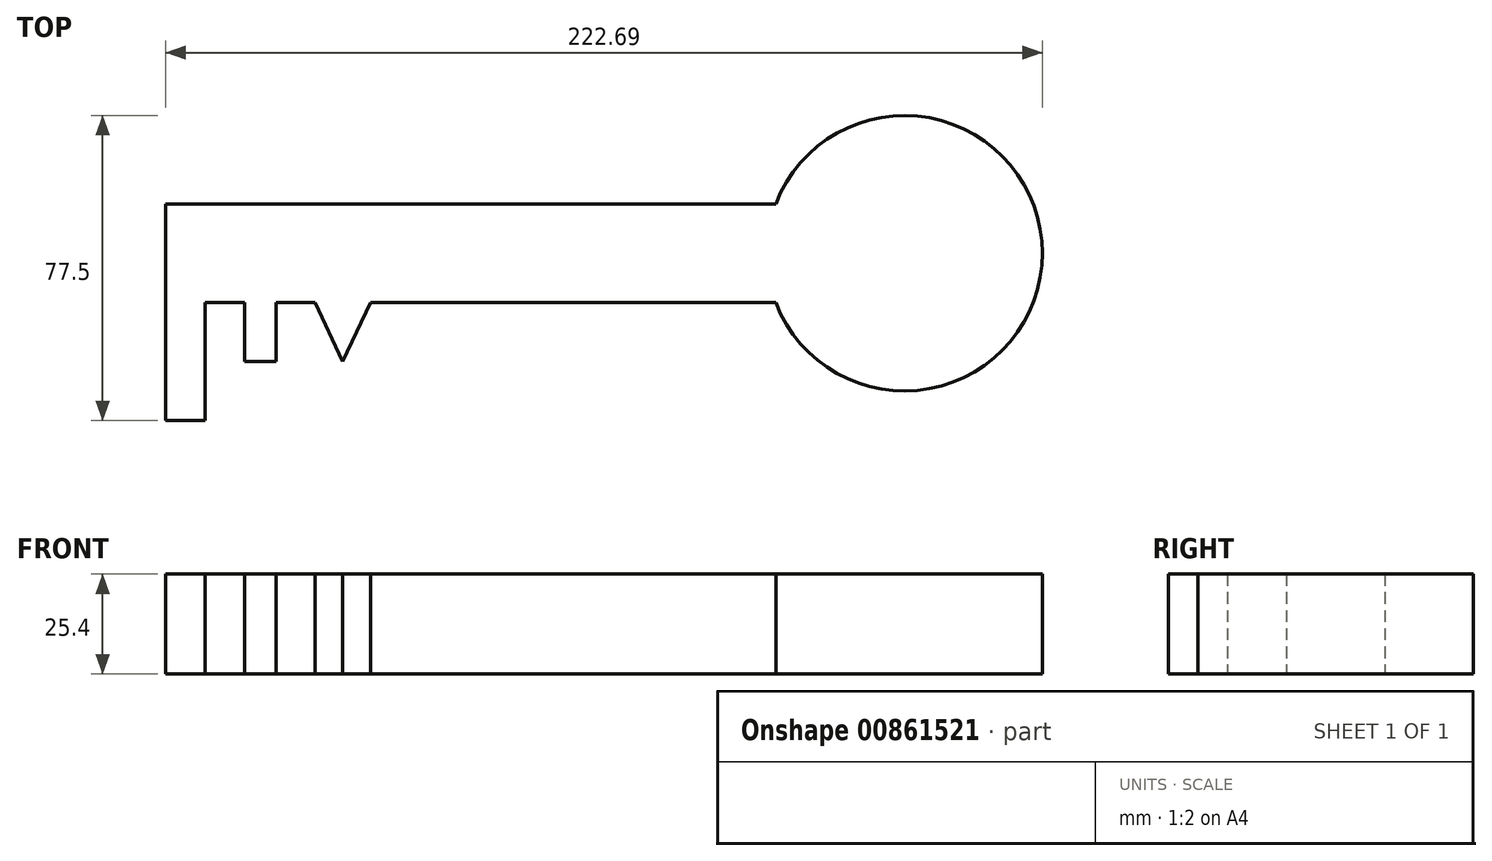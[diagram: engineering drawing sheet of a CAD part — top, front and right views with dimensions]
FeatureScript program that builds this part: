
annotation { "Feature Type Name" : "Feature", "Feature Type Description" : "" }
export const myFeature = defineFeature(function(context is Context, id is Id, definition is map)
    precondition{}
    {
        {
            var Q0;
            Q0=qCreatedBy(makeId("Top.planeOp"),FACE);
            var sketch = newSketch(context, id + "F0", { "sketchPlane" : qUnion([Q0])});
            skLineSegment(sketch, "E0.bottom", {"start": v(96.79, 26.03) * mm, "end": v(-58.21, 26.03) * mm});
            skLineSegment(sketch, "E0.top", {"start": v(96.79, 1.03) * mm, "end": v(-58.21, 1.03) * mm});
            skLineSegment(sketch, "E0.left", {"start": v(96.79, 26.03) * mm, "end": v(96.79, 1.03) * mm});
            skLineSegment(sketch, "E0.right", {"start": v(-58.21, 26.03) * mm, "end": v(-58.21, 1.03) * mm});
            skLineSegment(sketch, "E1.bottom", {"start": v(-58.21, 1.03) * mm, "end": v(-48.21, 1.03) * mm});
            skLineSegment(sketch, "E1.top", {"start": v(-58.21, -28.97) * mm, "end": v(-48.21, -28.97) * mm});
            skLineSegment(sketch, "E1.left", {"start": v(-58.21, 1.03) * mm, "end": v(-58.21, -28.97) * mm});
            skLineSegment(sketch, "E1.right", {"start": v(-48.21, 1.03) * mm, "end": v(-48.21, -28.97) * mm});
            skLineSegment(sketch, "E2.bottom", {"start": v(-30.21, 1.03) * mm, "end": v(-38.21, 1.03) * mm});
            skLineSegment(sketch, "E2.top", {"start": v(-30.21, -13.97) * mm, "end": v(-38.21, -13.97) * mm});
            skLineSegment(sketch, "E2.left", {"start": v(-30.21, 1.03) * mm, "end": v(-30.21, -13.97) * mm});
            skLineSegment(sketch, "E2.right", {"start": v(-38.21, 1.03) * mm, "end": v(-38.21, -13.97) * mm});
            skLineSegment(sketch, "E3", {"start": v(-20.21, 1.03) * mm, "end": v(-13.3, -13.97) * mm});
            skLineSegment(sketch, "E4", {"start": v(-13.3, -13.97) * mm, "end": v(-6.21, 1.03) * mm});
            skArc(sketch, "E5", {"start": v(96.79, 1.03) * mm, "mid": v(164.48, 13.53) * mm, "end": v(96.79, 26.03) * mm});
            skCircle(sketch, "E6", {"center": v(129.48, 13.53) * mm, "radius": 17.5 * mm});
            skLineSegment(sketch, "E7", {"start": v(129.48, 13.53) * mm, "end": v(-58.21, 13.53) * mm, "construction": true});
            skSolve(sketch);
        }
        {
            var Q0;
            Q0=makeQuery(id+"F0.imprint","IMPRINT",FACE,{"disambiguationData":[TD([[makeQuery(id+"F0.imprint","IMPRINT",EDGE,{"derivedFrom":sQuery(id+"F0.wireOp",EDGE,"E1.top")}),1.0]])]});
            var Q1;
            Q1=makeQuery(id+"F0.imprint","IMPRINT",FACE,{"disambiguationData":[TD([[makeQuery(id+"F0.imprint","IMPRINT",EDGE,{"derivedFrom":sQuery(id+"F0.wireOp",EDGE,"E2.top")}),-1.0]])]});
            var Q2;
            Q2=makeQuery(id+"F0.imprint","IMPRINT",FACE,{"disambiguationData":[TD([[makeQuery(id+"F0.imprint","IMPRINT",EDGE,{"derivedFrom":sQuery(id+"F0.wireOp",EDGE,"E0.bottom")}),1.0]])]});
            var Q3;
            {var subQ0=sQuery(id+"F0.wireOp",EDGE,"E3");Q3=makeQuery(id+"F0.imprint","IMPRINT",FACE,{"disambiguationData":[TD([[makeQuery(id+"F0.imprint","IMPRINT",EDGE,{"derivedFrom":subQ0}),1.0]])]});}
            var Q4;
            Q4=makeQuery(id+"F0.imprint","IMPRINT",FACE,{"disambiguationData":[TD([[makeQuery(id+"F0.imprint","IMPRINT",EDGE,{"derivedFrom":sQuery(id+"F0.wireOp",EDGE,"E6")}),1.0]])]});
            var Q5;
            Q5=makeQuery(id+"F0.imprint","IMPRINT",FACE,{"disambiguationData":[TD([[makeQuery(id+"F0.imprint","IMPRINT",EDGE,{"derivedFrom":sQuery(id+"F0.wireOp",EDGE,"E0.left")}),1.0]])]});
            extrude(context, id + "F1", {"entities" : qUnion([Q0, Q1, Q2, Q3, Q4, Q5]), "depth" : 25.4 * mm, "offsetDistance" : 25.4 * mm});
        }
    });
